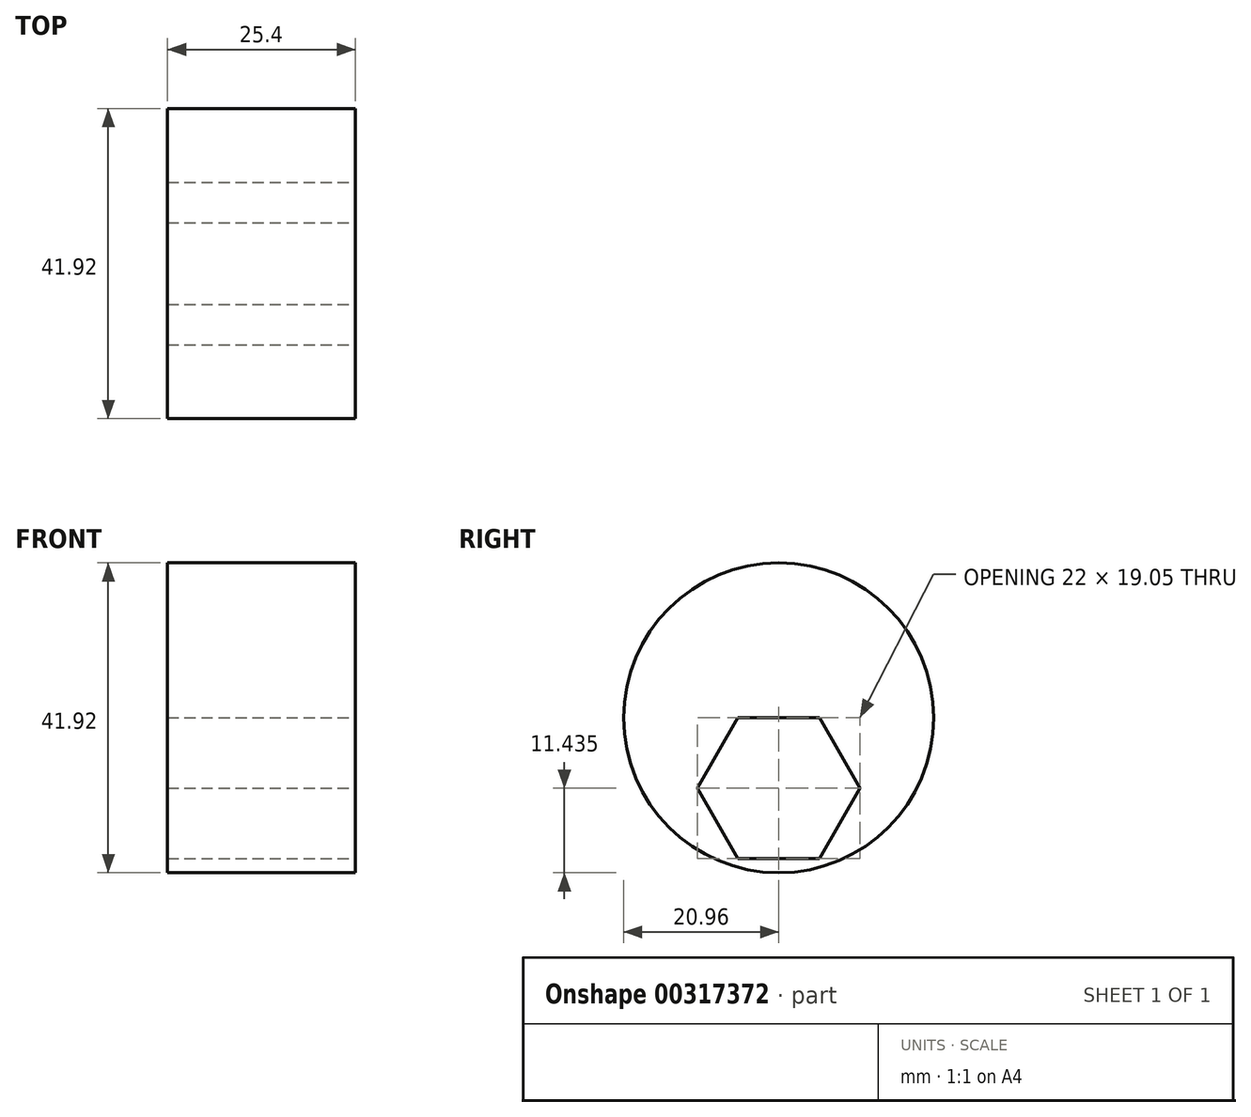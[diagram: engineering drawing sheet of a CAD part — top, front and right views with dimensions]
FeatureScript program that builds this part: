
annotation { "Feature Type Name" : "Feature", "Feature Type Description" : "" }
export const myFeature = defineFeature(function(context is Context, id is Id, definition is map)
    precondition{}
    {
        {
            var Q0;
            Q0=qCreatedBy(makeId("Right.planeOp"),FACE);
            var sketch = newSketch(context, id + "F0", { "sketchPlane" : qUnion([Q0])});
            skCircle(sketch, "E0", {"center": v(0, 0) * mm, "radius": 20.96 * mm});
            skSolve(sketch);
        }
        {
            var Q0;
            Q0=makeQuery(id+"F0.imprint","IMPRINT",FACE,{"disambiguationData":[TD([[makeQuery(id+"F0.imprint","IMPRINT",EDGE,{"derivedFrom":sQuery(id+"F0.wireOp",EDGE,"E0")}),1.0]])]});
            extrude(context, id + "F1", {"entities" : qUnion([Q0]), "depth" : 25.4 * mm});
        }
        {
            var Q0;
            Q0=makeQuery(id+"F1.opExtrude","CAP_FACE",FACE,{"disambiguationData":[OSD([sQuery(id+"F0.wireOp",EDGE,"E0")])],"isStart":false});
            var sketch = newSketch(context, id + "F2", { "sketchPlane" : qUnion([Q0])});
            skLineSegment(sketch, "E1", {"start": v(0, 0) * mm, "end": v(0, -19.05) * mm, "construction": true});
            skLineSegment(sketch, "E2", {"start": v(0, -19.05) * mm, "end": v(0, -9.53) * mm, "construction": true});
            skCircle(sketch, "E3.cCircle", {"center": v(0, -9.53) * mm, "radius": 9.53 * mm, "construction": true});
            skLineSegment(sketch, "E3.0", {"start": v(-5.5, 0) * mm, "end": v(5.5, 0) * mm});
            skLineSegment(sketch, "E3.1", {"start": v(5.5, 0) * mm, "end": v(11, -9.52) * mm});
            skLineSegment(sketch, "E3.2", {"start": v(11, -9.53) * mm, "end": v(5.5, -19.05) * mm});
            skLineSegment(sketch, "E3.3", {"start": v(5.5, -19.05) * mm, "end": v(-5.5, -19.05) * mm});
            skLineSegment(sketch, "E3.4", {"start": v(-5.5, -19.05) * mm, "end": v(-11, -9.53) * mm});
            skLineSegment(sketch, "E3.5", {"start": v(-11, -9.53) * mm, "end": v(-5.5, 0) * mm});
            skPoint(sketch, "E3.0.midPoint", {"position": v(0, 0) * mm});
            skSolve(sketch);
        }
        {
            var Q0;
            Q0=makeQuery(id+"F2.imprint","IMPRINT",FACE,{"disambiguationData":[TD([[makeQuery(id+"F2.imprint","IMPRINT",EDGE,{"derivedFrom":sQuery(id+"F2.wireOp",EDGE,"E3.0")}),-1.0]])]});
            extrude(context, id + "F3", {"entities" : qUnion([Q0]), "operationType" : NewBodyOperationType.REMOVE, "oppositeDirection" : true, "depth" : 25.4 * mm});
        }
    });
